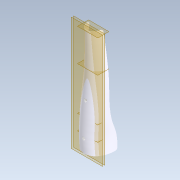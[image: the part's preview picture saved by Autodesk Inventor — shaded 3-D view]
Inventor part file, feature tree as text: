
AUTODESK INVENTOR PART (.ipt)
format: ipt  version: 2020.2 (Build 242310000, 310)  size: 410,112 bytes
history: native  units: mm
features: sketch x8, plane x6, extrude x3, loft x1, fillet x1, chamfer x1
ambient origin geometry x8: Origin, YZ Plane, XZ Plane, XY Plane, X Axis, Y Axis, Z Axis, Center Point
bodies: Solid1 (feature_tree)
feature tree (20):
  plane  "Work Plane1"
  plane  "Work Plane2"
  plane  "Work Plane3"
  plane  "Work Plane4"
  loft  "Loft1"
  fillet  "Fillet1"  Radius=35.0mm
  plane  "Work Plane5"
  extrude  "Extrusion1"  Depth=100.0mm
  extrude  "Extrusion2"  TaperAngle=0.0deg  [1 undecoded]
  plane  "Work Plane6"
  extrude  "Extrusion3"  Depth=1.0mm
  chamfer  "Chamfer1"  Distance=30.0mm
  sketch  "Sketch1"  dims[d5=30.0mm d7=210.0mm d9=35.0mm]
  sketch  "Sketch2"  dims[d10=1.0mm]
  sketch  "Sketch3"  dims[d11=0.0mm d12=90.0deg d13=0.0mm d14=90.0deg d15=0.0mm d16=90.0deg d17=0.0mm d18=90.0deg d19=100.0mm]
  sketch  "Sketch4"  dims[d20=1.0mm d21=0.0mm d22=90.0deg]
  sketch  "Sketch5"  dims[d23=1.0mm d24=1.0mm]
  sketch  "Sketch6"  dims[d25=1.0mm]
  sketch  "Sketch7"  dims[d26=5.0mm]
  sketch  "Sketch8"  dims[d27=20.0mm d28=30.0mm d29=10.0mm d30=75.0mm d31=10.0mm d32=31.066mm d33=0.0mm d34=3.0mm d35=3.0mm d36=10.0mm d37=0.0mm d38=5.0mm d39=7.0mm d40=7.0mm d41=26.066mm d42=0.0mm d43=5.0mm d44=2.0mm d45=45.0deg]
note: 1 required parameter value undecoded (feature->parameter linkage not recoverable at this tier; creation-order binding heuristic only, values carry confidence <= 0.55)
